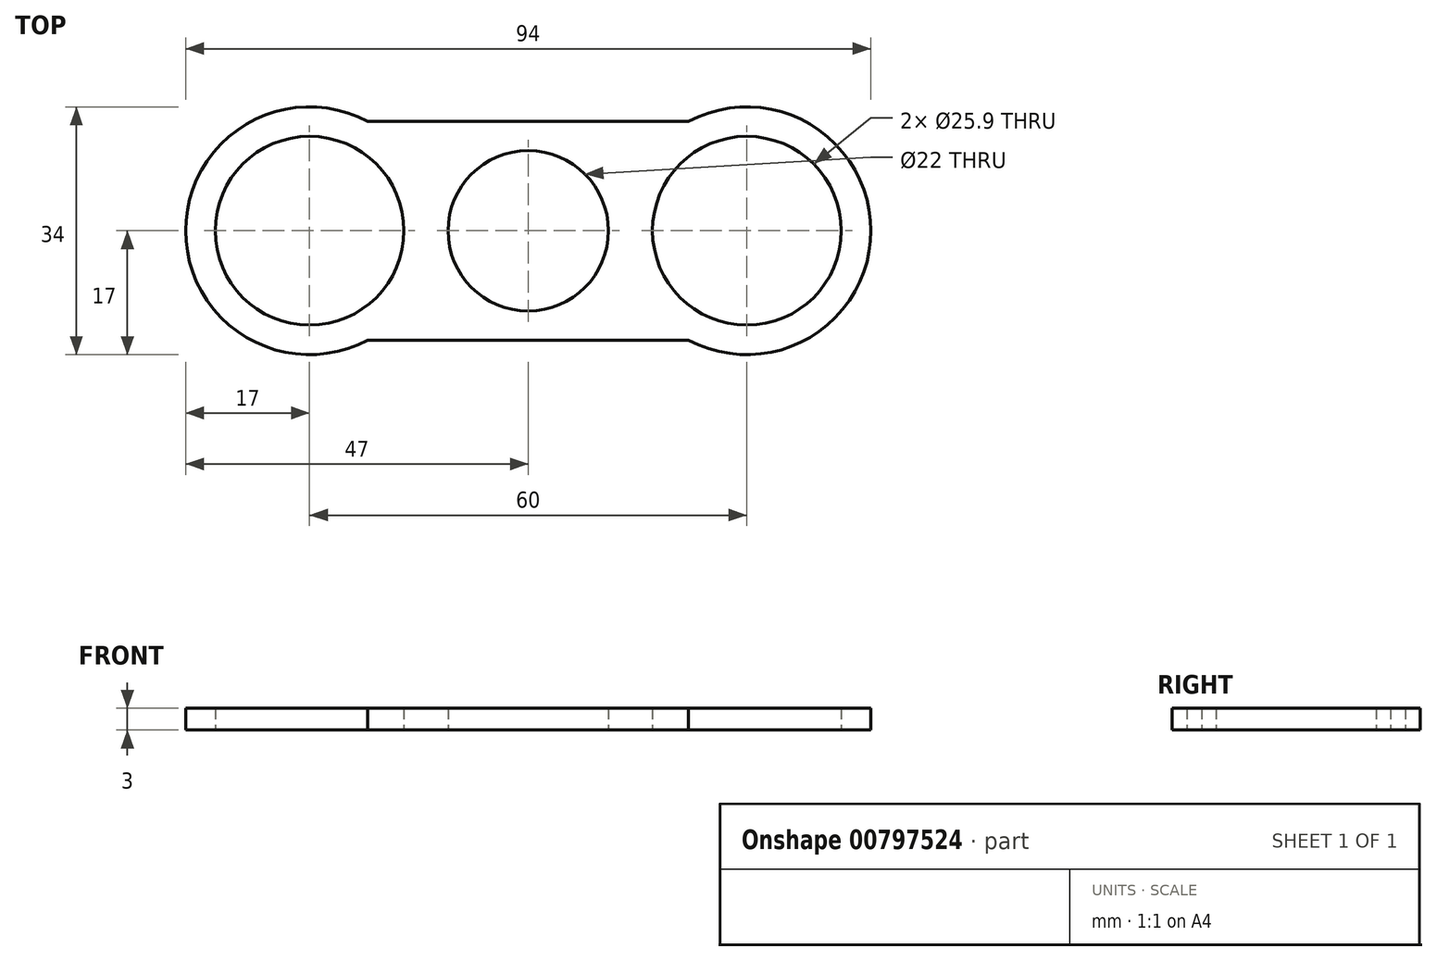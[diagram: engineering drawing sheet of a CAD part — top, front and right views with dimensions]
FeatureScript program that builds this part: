
annotation { "Feature Type Name" : "Feature", "Feature Type Description" : "" }
export const myFeature = defineFeature(function(context is Context, id is Id, definition is map)
    precondition{}
    {
        {
            var Q0;
            Q0=qCreatedBy(makeId("Top.planeOp"),FACE);
            var sketch = newSketch(context, id + "F0", { "sketchPlane" : qUnion([Q0])});
            skArc(sketch, "E0", {"start": v(0, -11) * mm, "mid": v(11, 0) * mm, "end": v(0, 11) * mm});
            skCircle(sketch, "E1", {"center": v(30, 0) * mm, "radius": 12.95 * mm});
            skArc(sketch, "E2", {"start": v(22, -15) * mm, "mid": v(47, 0) * mm, "end": v(22, 15) * mm});
            skArc(sketch, "E3.1.1", {"start": v(0, 11) * mm, "mid": v(-11, 0) * mm, "end": v(0, -11) * mm});
            skArc(sketch, "E3.1.3", {"start": v(-22, 15) * mm, "mid": v(-47, 0) * mm, "end": v(-22, -15) * mm});
            skLineSegment(sketch, "E4", {"start": v(-22, -15) * mm, "end": v(22, -15) * mm});
            skLineSegment(sketch, "E5", {"start": v(22, 15) * mm, "end": v(-22, 15) * mm});
            skCircle(sketch, "E6", {"center": v(-30, 0) * mm, "radius": 12.95 * mm});
            skSolve(sketch);
        }
        {
            var Q0;
            Q0 = qSketchRegion(id + "F0", true);
            extrude(context, id + "F1", {"entities" : qUnion([Q0]), "depth" : 3 * mm, "offsetDistance" : 25 * mm});
        }
    });
